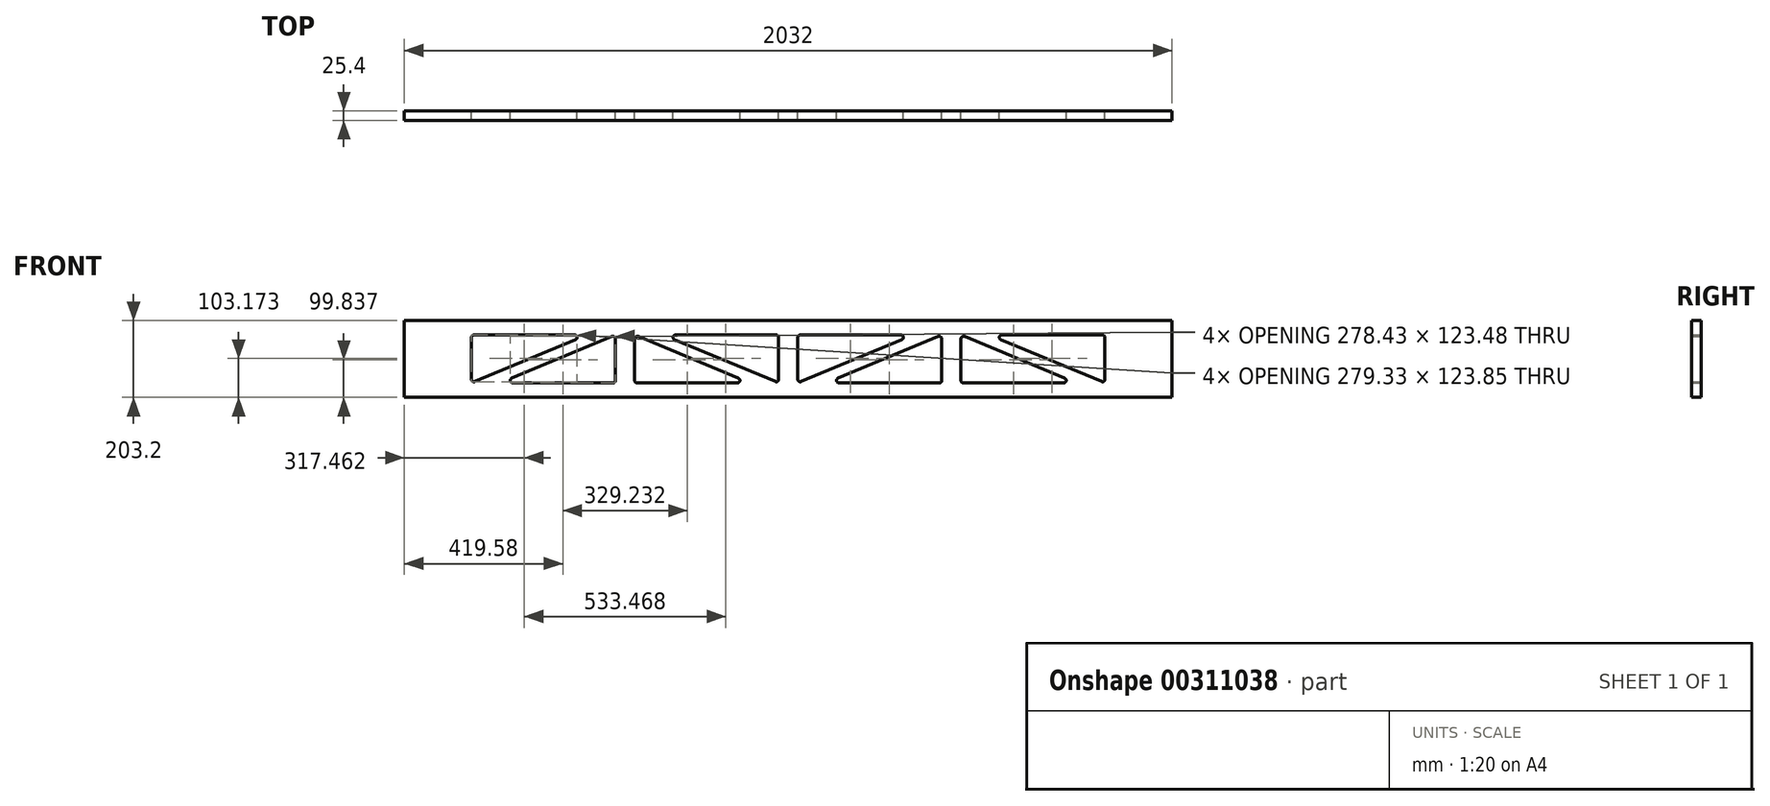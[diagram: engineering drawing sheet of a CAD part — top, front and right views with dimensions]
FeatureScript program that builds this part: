
annotation { "Feature Type Name" : "Feature", "Feature Type Description" : "" }
export const myFeature = defineFeature(function(context is Context, id is Id, definition is map)
    precondition{}
    {
        {
            var Q0;
            Q0=qCreatedBy(makeId("Front.planeOp"),FACE);
            var sketch = newSketch(context, id + "F0", { "sketchPlane" : qUnion([Q0])});
            skLineSegment(sketch, "E0.bottom", {"start": v(-101.8, 174.09) * mm, "end": v(1930.2, 174.09) * mm});
            skLineSegment(sketch, "E0.top", {"start": v(-101.8, -29.11) * mm, "end": v(1930.2, -29.11) * mm});
            skLineSegment(sketch, "E0.left", {"start": v(-101.8, 174.09) * mm, "end": v(-101.8, -29.11) * mm});
            skLineSegment(sketch, "E0.right", {"start": v(1930.2, 174.09) * mm, "end": v(1930.2, -29.11) * mm});
            skLineSegment(sketch, "E1", {"start": v(914.2, 174.09) * mm, "end": v(914.2, -29.11) * mm, "construction": true});
            skLineSegment(sketch, "E2", {"start": v(939.6, 129.64) * mm, "end": v(939.6, 18.35) * mm});
            skLineSegment(sketch, "E3", {"start": v(945.95, 135.99) * mm, "end": v(1212.65, 135.99) * mm});
            skLineSegment(sketch, "E4", {"start": v(1215.09, 123.78) * mm, "end": v(948.23, 12.59) * mm});
            skLineSegment(sketch, "E5", {"start": v(1320.6, 125.52) * mm, "end": v(1320.6, 15.34) * mm});
            skLineSegment(sketch, "E6", {"start": v(1314.25, 8.99) * mm, "end": v(1048.67, 8.99) * mm});
            skLineSegment(sketch, "E7", {"start": v(1046.14, 21.63) * mm, "end": v(1310.93, 131.96) * mm});
            skPoint(sketch, "E8.visualSharp", {"position": v(939.6, 135.99) * mm});
            skArc(sketch, "E8.filletArc", {"start": v(945.95, 135.99) * mm, "mid": v(941.46, 134.13) * mm, "end": v(939.6, 129.64) * mm});
            skPoint(sketch, "E9.visualSharp", {"position": v(939.6, 8.99) * mm});
            skArc(sketch, "E9.filletArc", {"start": v(939.6, 18.26) * mm, "mid": v(942.41, 13.13) * mm, "end": v(948.23, 12.59) * mm});
            skArc(sketch, "E10.filletArc", {"start": v(939.6, 18.35) * mm, "mid": v(942.37, 13.16) * mm, "end": v(948.23, 12.59) * mm});
            skPoint(sketch, "E11.visualSharp", {"position": v(1244.4, 135.99) * mm});
            skArc(sketch, "E11.filletArc", {"start": v(1215.09, 123.78) * mm, "mid": v(1218.87, 130.88) * mm, "end": v(1212.65, 135.99) * mm});
            skPoint(sketch, "E12.visualSharp", {"position": v(1320.6, 135.99) * mm});
            skArc(sketch, "E12.filletArc", {"start": v(1320.6, 125.52) * mm, "mid": v(1317.49, 131.33) * mm, "end": v(1310.93, 131.96) * mm});
            skPoint(sketch, "E13.visualSharp", {"position": v(1320.6, 8.99) * mm});
            skArc(sketch, "E13.filletArc", {"start": v(1314.25, 8.99) * mm, "mid": v(1318.74, 10.85) * mm, "end": v(1320.6, 15.34) * mm});
            skPoint(sketch, "E14.visualSharp", {"position": v(1015.8, 8.99) * mm});
            skArc(sketch, "E14.filletArc", {"start": v(1046.14, 21.63) * mm, "mid": v(1042.22, 14.27) * mm, "end": v(1048.67, 8.99) * mm});
            skLineSegment(sketch, "E15", {"start": v(1346, 174.09) * mm, "end": v(1346, -29.11) * mm, "construction": true});
            skArc(sketch, "E16.MirrorCS", {"start": v(1752.4, 18.35) * mm, "mid": v(1749.62, 13.16) * mm, "end": v(1743.76, 12.59) * mm});
            skArc(sketch, "E17.MirrorCS", {"start": v(1746.05, 135.99) * mm, "mid": v(1750.54, 134.13) * mm, "end": v(1752.4, 129.64) * mm});
            skArc(sketch, "E18.MirrorCS", {"start": v(1377.75, 8.99) * mm, "mid": v(1373.26, 10.85) * mm, "end": v(1371.4, 15.34) * mm});
            skArc(sketch, "E19.MirrorCS", {"start": v(1645.85, 21.63) * mm, "mid": v(1649.77, 14.27) * mm, "end": v(1643.32, 8.99) * mm});
            skArc(sketch, "E20.MirrorCS", {"start": v(1752.4, 18.26) * mm, "mid": v(1749.58, 13.13) * mm, "end": v(1743.76, 12.59) * mm});
            skArc(sketch, "E21.MirrorCS", {"start": v(1476.9, 123.78) * mm, "mid": v(1473.12, 130.88) * mm, "end": v(1479.35, 135.99) * mm});
            skArc(sketch, "E22.MirrorCS", {"start": v(1371.4, 125.52) * mm, "mid": v(1374.5, 131.33) * mm, "end": v(1381.06, 131.96) * mm});
            skPoint(sketch, "E23.MirrorP", {"position": v(1447.6, 135.99) * mm});
            skLineSegment(sketch, "E24.MirrorCS", {"start": v(1752.4, 129.64) * mm, "end": v(1752.4, 18.35) * mm});
            skPoint(sketch, "E25.MirrorP", {"position": v(1752.4, 8.99) * mm});
            skLineSegment(sketch, "E26.MirrorCS", {"start": v(1746.05, 135.99) * mm, "end": v(1479.35, 135.99) * mm});
            skLineSegment(sketch, "E27.MirrorCS", {"start": v(1476.9, 123.78) * mm, "end": v(1743.76, 12.59) * mm});
            skLineSegment(sketch, "E28.MirrorCS", {"start": v(1371.4, 125.52) * mm, "end": v(1371.4, 15.34) * mm});
            skLineSegment(sketch, "E29.MirrorCS", {"start": v(1377.75, 8.99) * mm, "end": v(1643.32, 8.99) * mm});
            skLineSegment(sketch, "E30.MirrorCS", {"start": v(1645.85, 21.63) * mm, "end": v(1381.06, 131.96) * mm});
            skPoint(sketch, "E31.MirrorP", {"position": v(1371.4, 8.99) * mm});
            skPoint(sketch, "E32.MirrorP", {"position": v(1752.4, 135.99) * mm});
            skPoint(sketch, "E33.MirrorP", {"position": v(1371.4, 135.99) * mm});
            skPoint(sketch, "E34.MirrorP", {"position": v(1676.2, 8.99) * mm});
            skArc(sketch, "E35.MirrorCS", {"start": v(450.65, 8.99) * mm, "mid": v(455.14, 10.85) * mm, "end": v(457, 15.34) * mm});
            skArc(sketch, "E36.MirrorCS", {"start": v(76, 18.35) * mm, "mid": v(78.77, 13.16) * mm, "end": v(84.63, 12.59) * mm});
            skArc(sketch, "E37.MirrorCS", {"start": v(882.45, 135.99) * mm, "mid": v(886.94, 134.13) * mm, "end": v(888.8, 129.64) * mm});
            skArc(sketch, "E38.MirrorCS", {"start": v(782.25, 21.63) * mm, "mid": v(786.17, 14.27) * mm, "end": v(779.72, 8.99) * mm});
            skArc(sketch, "E39.MirrorCS", {"start": v(182.54, 21.63) * mm, "mid": v(178.62, 14.27) * mm, "end": v(185.07, 8.99) * mm});
            skArc(sketch, "E40.MirrorCS", {"start": v(76, 18.26) * mm, "mid": v(78.81, 13.13) * mm, "end": v(84.63, 12.59) * mm});
            skArc(sketch, "E41.MirrorCS", {"start": v(514.15, 8.99) * mm, "mid": v(509.66, 10.85) * mm, "end": v(507.8, 15.34) * mm});
            skArc(sketch, "E42.MirrorCS", {"start": v(82.35, 135.99) * mm, "mid": v(77.86, 134.13) * mm, "end": v(76, 129.64) * mm});
            skArc(sketch, "E43.MirrorCS", {"start": v(888.8, 18.26) * mm, "mid": v(885.98, 13.13) * mm, "end": v(880.16, 12.59) * mm});
            skArc(sketch, "E44.MirrorCS", {"start": v(888.8, 18.35) * mm, "mid": v(886.02, 13.16) * mm, "end": v(880.16, 12.59) * mm});
            skArc(sketch, "E45.MirrorCS", {"start": v(351.49, 123.78) * mm, "mid": v(355.27, 130.88) * mm, "end": v(349.05, 135.99) * mm});
            skArc(sketch, "E46.MirrorCS", {"start": v(457, 125.52) * mm, "mid": v(453.89, 131.33) * mm, "end": v(447.33, 131.96) * mm});
            skArc(sketch, "E47.MirrorCS", {"start": v(507.8, 125.52) * mm, "mid": v(510.9, 131.33) * mm, "end": v(517.46, 131.96) * mm});
            skArc(sketch, "E48.MirrorCS", {"start": v(613.3, 123.78) * mm, "mid": v(609.52, 130.88) * mm, "end": v(615.75, 135.99) * mm});
            skPoint(sketch, "E49.MirrorP", {"position": v(76, 8.99) * mm});
            skLineSegment(sketch, "E50.MirrorCS", {"start": v(351.49, 123.78) * mm, "end": v(84.63, 12.59) * mm});
            skLineSegment(sketch, "E51.MirrorCS", {"start": v(450.65, 8.99) * mm, "end": v(185.07, 8.99) * mm});
            skPoint(sketch, "E52.MirrorP", {"position": v(457, 135.99) * mm});
            skPoint(sketch, "E53.MirrorP", {"position": v(380.8, 135.99) * mm});
            skPoint(sketch, "E54.MirrorP", {"position": v(888.8, 8.99) * mm});
            skPoint(sketch, "E55.MirrorP", {"position": v(457, 8.99) * mm});
            skLineSegment(sketch, "E56.MirrorCS", {"start": v(182.54, 21.63) * mm, "end": v(447.33, 131.96) * mm});
            skPoint(sketch, "E57.MirrorP", {"position": v(152.2, 8.99) * mm});
            skPoint(sketch, "E58.MirrorP", {"position": v(507.8, 8.99) * mm});
            skLineSegment(sketch, "E59.MirrorCS", {"start": v(888.8, 129.64) * mm, "end": v(888.8, 18.35) * mm});
            skPoint(sketch, "E60.MirrorP", {"position": v(888.8, 135.99) * mm});
            skLineSegment(sketch, "E61.MirrorCS", {"start": v(457, 125.52) * mm, "end": v(457, 15.34) * mm});
            skLineSegment(sketch, "E62.MirrorCS", {"start": v(514.15, 8.99) * mm, "end": v(779.72, 8.99) * mm});
            skPoint(sketch, "E63.MirrorP", {"position": v(584, 135.99) * mm});
            skLineSegment(sketch, "E64.MirrorCS", {"start": v(82.35, 135.99) * mm, "end": v(349.05, 135.99) * mm});
            skLineSegment(sketch, "E65.MirrorCS", {"start": v(76, 129.64) * mm, "end": v(76, 18.35) * mm});
            skPoint(sketch, "E66.MirrorP", {"position": v(507.8, 135.99) * mm});
            skLineSegment(sketch, "E67.MirrorCS", {"start": v(782.25, 21.63) * mm, "end": v(517.46, 131.96) * mm});
            skPoint(sketch, "E68.MirrorP", {"position": v(76, 135.99) * mm});
            skLineSegment(sketch, "E69.MirrorCS", {"start": v(882.45, 135.99) * mm, "end": v(615.75, 135.99) * mm});
            skPoint(sketch, "E70.MirrorP", {"position": v(812.6, 8.99) * mm});
            skLineSegment(sketch, "E71.MirrorCS", {"start": v(507.8, 125.52) * mm, "end": v(507.8, 15.34) * mm});
            skLineSegment(sketch, "E72.MirrorCS", {"start": v(613.3, 123.78) * mm, "end": v(880.16, 12.59) * mm});
            skSolve(sketch);
        }
        {
            var Q0;
            Q0=makeQuery(id+"F0.imprint","IMPRINT",FACE,{"disambiguationData":[TD([[makeQuery(id+"F0.imprint","IMPRINT",EDGE,{"derivedFrom":sQuery(id+"F0.wireOp",EDGE,"E0.bottom")}),-1.0]])]});
            extrude(context, id + "F1", {"entities" : qUnion([Q0]), "depth" : 25.4 * mm});
        }
    });
